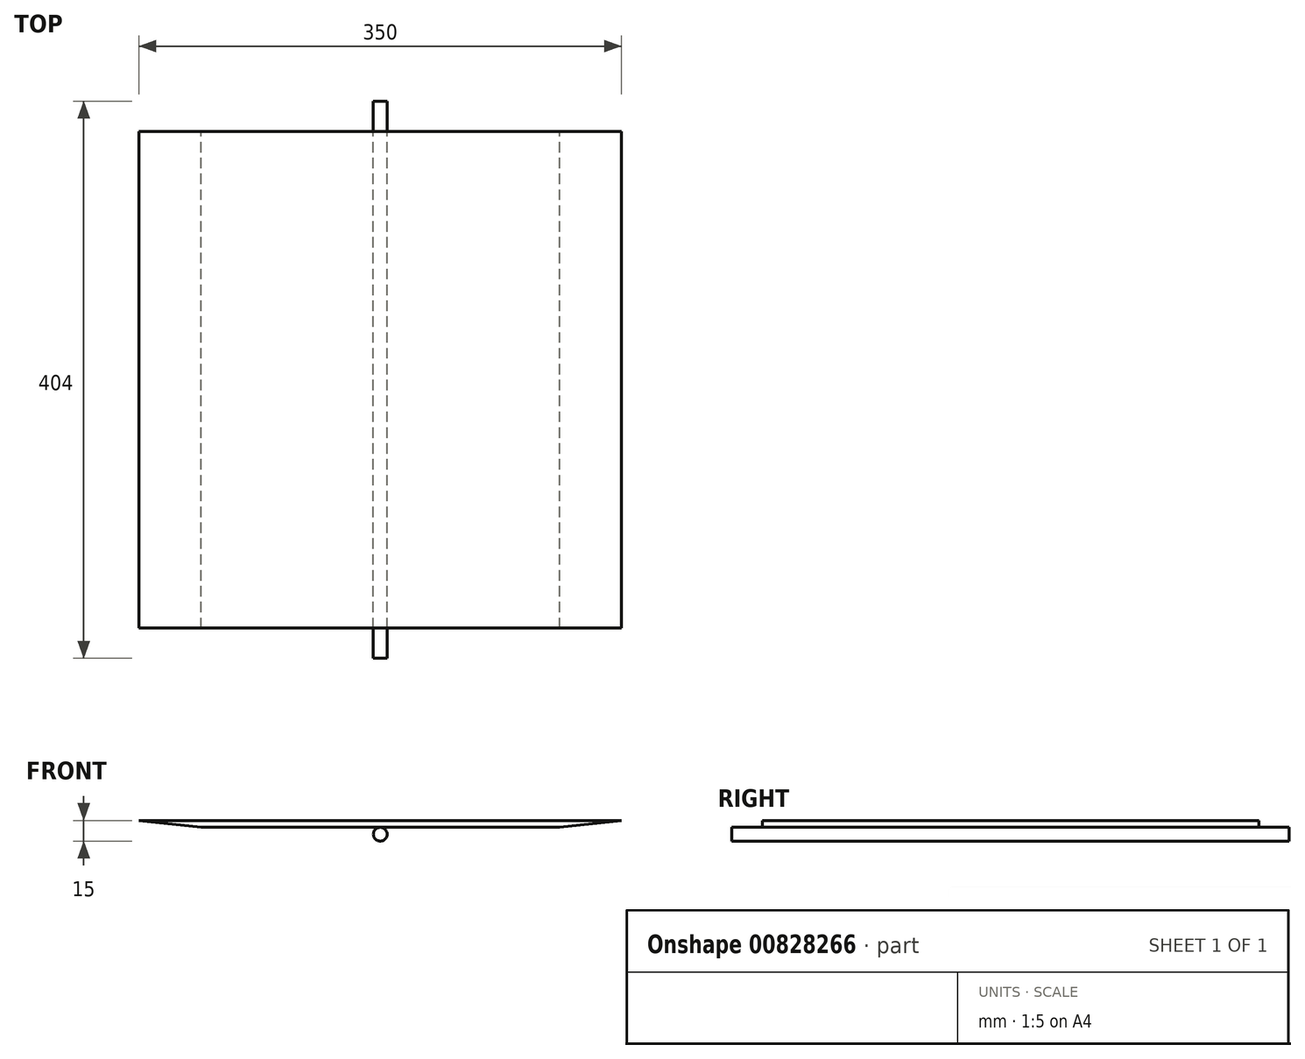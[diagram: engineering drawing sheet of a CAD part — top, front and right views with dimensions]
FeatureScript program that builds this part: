
annotation { "Feature Type Name" : "Feature", "Feature Type Description" : "" }
export const myFeature = defineFeature(function(context is Context, id is Id, definition is map)
    precondition{}
    {
        {
            var Q0;
            Q0=qCreatedBy(makeId("Front.planeOp"),FACE);
            var sketch = newSketch(context, id + "F0", { "sketchPlane" : qUnion([Q0])});
            skLineSegment(sketch, "E0", {"start": v(-130, 0) * mm, "end": v(130, 0) * mm});
            skLineSegment(sketch, "E1", {"start": v(130, 0) * mm, "end": v(175, 5) * mm});
            skLineSegment(sketch, "E2", {"start": v(175, 5) * mm, "end": v(-175, 5) * mm});
            skLineSegment(sketch, "E3", {"start": v(-175, 5) * mm, "end": v(-130, 0) * mm});
            skSolve(sketch);
        }
        {
            var Q0;
            Q0=makeQuery(id+"F0.imprint","IMPRINT",FACE,{"disambiguationData":[TD([[makeQuery(id+"F0.imprint","IMPRINT",EDGE,{"derivedFrom":sQuery(id+"F0.wireOp",EDGE,"E0")}),1.0]])]});
            extrude(context, id + "F1", {"entities" : qUnion([Q0]), "endBound" : BoundingType.SYMMETRIC, "depth" : 360 * mm, "offsetDistance" : 25 * mm});
        }
        {
            var Q0;
            Q0=qCreatedBy(makeId("Front.planeOp"),FACE);
            var sketch = newSketch(context, id + "F2", { "sketchPlane" : qUnion([Q0])});
            skCircle(sketch, "E4", {"center": v(0, -5) * mm, "radius": 5 * mm});
            skSolve(sketch);
        }
        {
            var Q0;
            Q0=makeQuery(id+"F2.imprint","IMPRINT",FACE,{"disambiguationData":[TD([[makeQuery(id+"F2.imprint","IMPRINT",EDGE,{"derivedFrom":sQuery(id+"F2.wireOp",EDGE,"E4")}),1.0]])]});
            extrude(context, id + "F3", {"entities" : qUnion([Q0]), "endBound" : BoundingType.SYMMETRIC, "depth" : 404 * mm, "offsetDistance" : 25 * mm});
        }
    });
